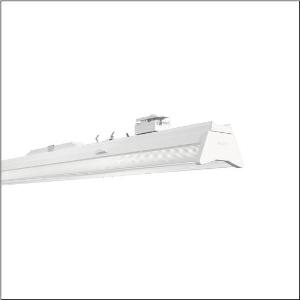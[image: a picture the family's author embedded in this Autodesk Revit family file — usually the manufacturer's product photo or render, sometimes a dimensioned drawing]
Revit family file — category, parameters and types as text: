
# Revit family: licross_r__11_performance_mo_51td167n485g_c044
name_source: partatom
category: Lighting Fixtures
units: mm (PartAtom-declared; Revit-internal decimal feet)

## family parameters
Cut with Voids When Loaded = No
Host = Face
Light Source = No
Part Type = Normal
Room Calculation Point = No
Round Connector Dimension = Use Diameter
Shared = No

## types (1)
- Licross® 11 Performance MO (1 x LED, 8840 lm, 48.6 W, 4000K)
    Apparent Load = 49 VA
    CIE Flux Codes = 66 88 96 79 100
    Color Rendering = 80
    Color Temperature = 4000K
    Default Elevation = 1800 mm
    Description = Licross® 11 Performance MO, luminaire insert, of sheet steel, galvanised, coil coated, white, length: 1.500mm, width: 120mm, height: 123mm, LED rated luminous flux: 8.840lm, light colour: 840, control gear: ON/OFF, with plug, 3-pole, with phase selection, mains connection: 220..240V, AC, 50/60Hz, rated input power: 49W, halogen-free wiring, primary light control with lens, of plastic, primary optical cover: cover, of PMMA, light emission: direct/indirect distribution, primary light characteristic: symmetric, protection rating (complete): IP54, insulation class (complete): insulation class I (protective earthing), certification: CE, ENEC, VDE, UKCA, protection symbol: D if used in an environment with non-conductive dust loads with corresponding accessories, impact resistance: IK06, permissible ambient temperature for indoor applications: -25..+35°C, corresponds to IFS (International Featured Standards) requirements for safety and quality in the food industry, reducing of maximum allowable ambient temperature of 5°C with ceiling mounting, LABS conformity tested according to VDMA 24364:2018-05, packaging unit: 1 piece
    Height = 114 mm
    Lamp = 1 x LED
    Lamp Light Flux = 8840 lm
    Lamp Power = 48.6 W
    Lamp count = 1
    Length = 1500 mm
    Luminous efficacy = 182 lm/W
    Manufacturer = Siteco
    ModVariant = No
    Model = 51TD167N485G
    Mounting Place = Ceiling
    Mounting Type = Pendant
    Number of Poles = 1
    OnlyDefault = Yes
    Power Factor = 1
    Product Name = Licross® 11 Performance MO
    Product group = luminaire insert
    ProductGroupID = 901
    Protection Class = Protection class I
    Protection Degree = IP 54
    RLX_Detail_Level = 1
    RLX_Emergency_Light_Flux = 0 lm
    RLX_Emergency_Type = 0
    RLX_Emergency_Type_DB = No
    RlxData = <blob elided: 30445 chars, md5=124438aa>
    Socket = socket
    Standby Power = 0 W
    System Light Flux = 8840 lm
    System Power = 49 W
    Type Comments = Product without accessories
    Type Image = l_1256138.jpg
    URL = http://relux.com
    VarID = ---
    Voltage = 0 V
    Weight = 0.00 kg
    Width = 120 mm

## geometry (parser evidence)
native form markers: Blend x4, Sweep x12
no freeform markers — native parametric forms only
